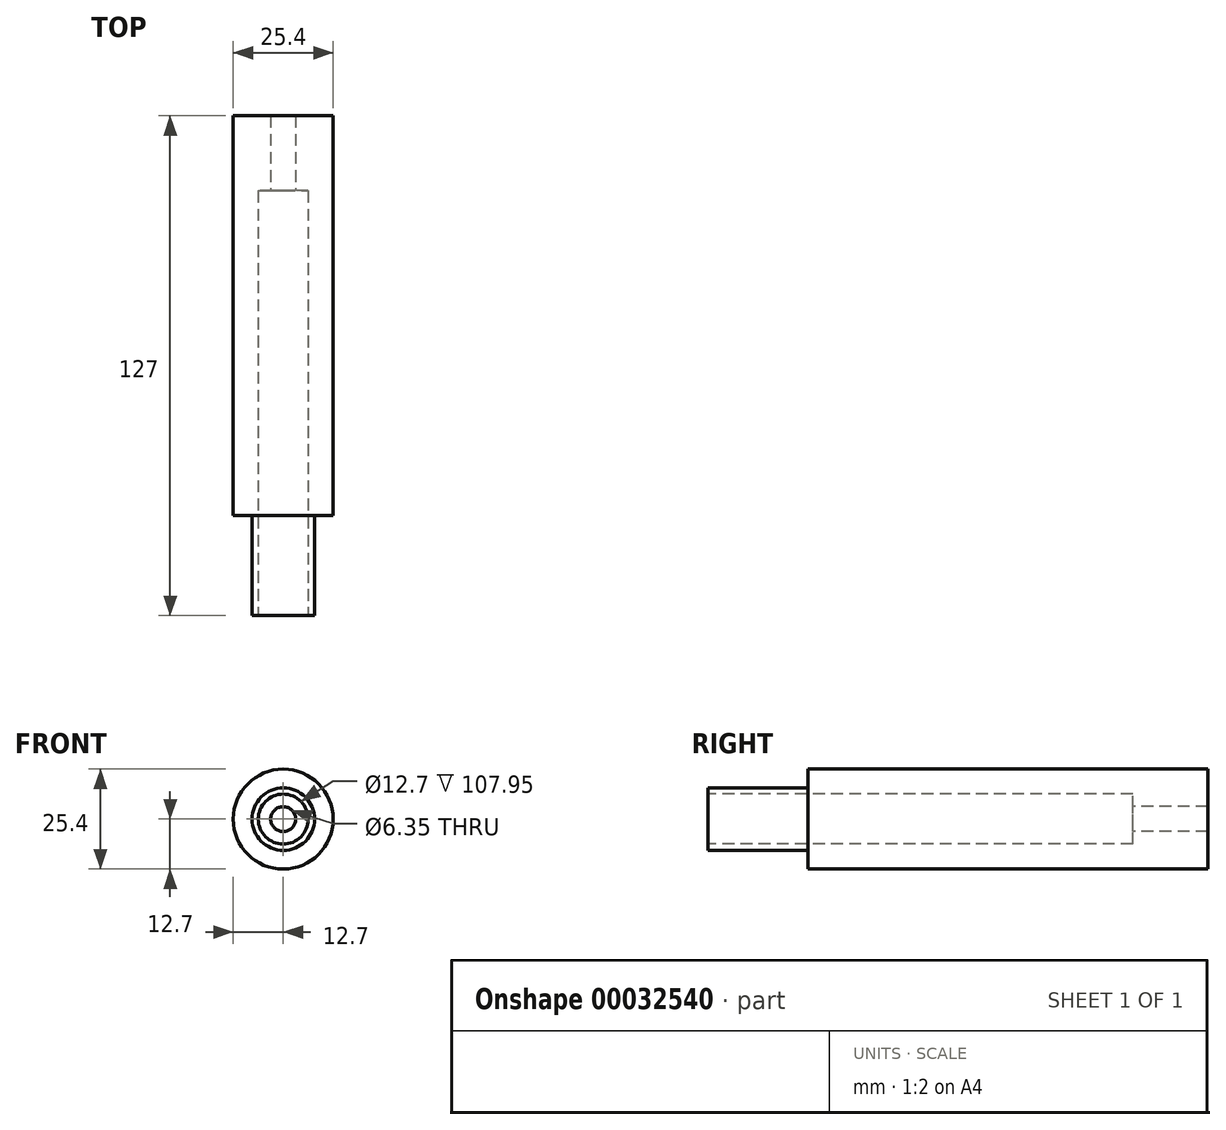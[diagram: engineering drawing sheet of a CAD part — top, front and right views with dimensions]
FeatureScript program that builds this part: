
annotation { "Feature Type Name" : "Feature", "Feature Type Description" : "" }
export const myFeature = defineFeature(function(context is Context, id is Id, definition is map)
    precondition{}
    {
        {
            var Q0;
            Q0=qCreatedBy(makeId("Right.planeOp"),FACE);
            var sketch = newSketch(context, id + "F0", { "sketchPlane" : qUnion([Q0])});
            skLineSegment(sketch, "E0", {"start": v(-127, 7.94) * mm, "end": v(-101.6, 7.94) * mm});
            skLineSegment(sketch, "E1", {"start": v(-101.6, 7.94) * mm, "end": v(-101.6, 12.7) * mm});
            skLineSegment(sketch, "E2", {"start": v(-101.6, 12.7) * mm, "end": v(0, 12.7) * mm});
            skLineSegment(sketch, "E3", {"start": v(0, 12.7) * mm, "end": v(0, 3.17) * mm});
            skLineSegment(sketch, "E4", {"start": v(0, 3.17) * mm, "end": v(-19.05, 3.17) * mm});
            skLineSegment(sketch, "E5", {"start": v(-19.05, 3.17) * mm, "end": v(-19.05, 6.35) * mm});
            skLineSegment(sketch, "E6", {"start": v(-19.05, 6.35) * mm, "end": v(-127, 6.35) * mm});
            skLineSegment(sketch, "E7", {"start": v(-127, 6.35) * mm, "end": v(-127, 7.94) * mm});
            skLineSegment(sketch, "E8", {"start": v(-78.03, 0) * mm, "end": v(0, 0) * mm, "construction": true});
            skSolve(sketch);
        }
        {
            var Q0;
            Q0 = qSketchRegion(id + "F0", true);
            var Q1;
            Q1=sQuery(id+"F0.wireOp",EDGE,"E8");
            revolve(context, id + "F1", {"entities" : qUnion([Q0]), "axis" : qUnion([Q1]), "revolveType" : RevolveType.FULL});
        }
    });
